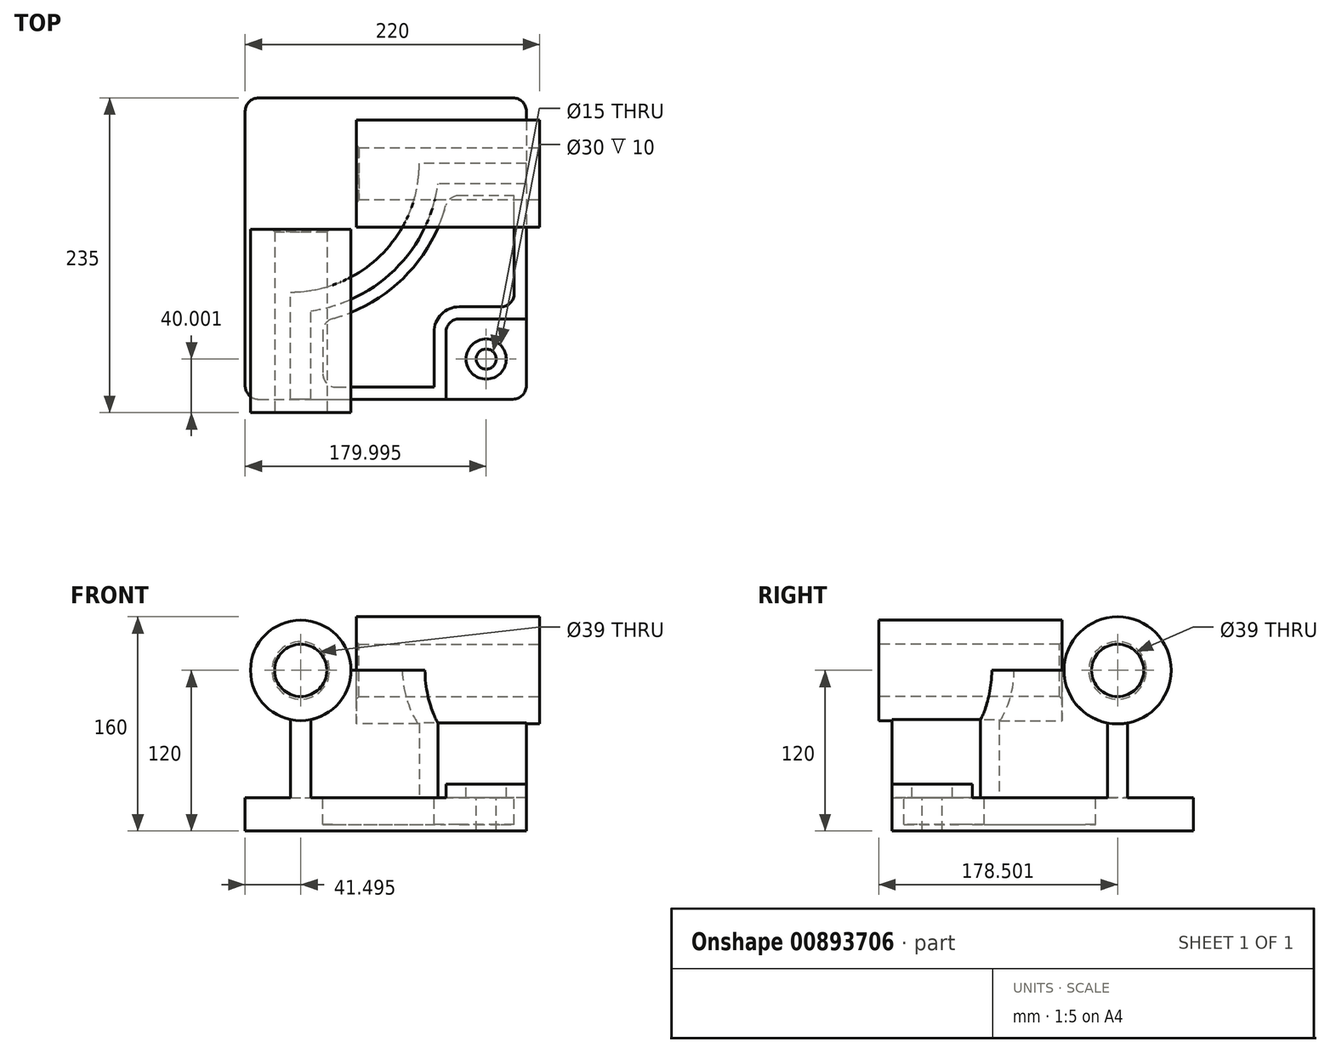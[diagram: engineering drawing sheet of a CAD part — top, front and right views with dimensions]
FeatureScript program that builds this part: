
annotation { "Feature Type Name" : "Feature", "Feature Type Description" : "" }
export const myFeature = defineFeature(function(context is Context, id is Id, definition is map)
    precondition{}
    {
        {
            var Q0;
            Q0=qCreatedBy(makeId("Top.planeOp"),FACE);
            var sketch = newSketch(context, id + "F0", { "sketchPlane" : qUnion([Q0])});
            skLineSegment(sketch, "E0.bottom", {"start": v(-141.63, 109.9) * mm, "end": v(68.37, 109.9) * mm});
            skLineSegment(sketch, "E0.top", {"start": v(-141.63, -115.1) * mm, "end": v(68.37, -115.1) * mm});
            skLineSegment(sketch, "E0.left", {"start": v(-141.63, 109.9) * mm, "end": v(-141.63, -115.1) * mm});
            skLineSegment(sketch, "E0.right", {"start": v(68.37, 109.9) * mm, "end": v(68.37, -115.1) * mm});
            skSolve(sketch);
        }
        {
            var Q0;
            Q0=makeQuery(id+"F0.imprint","IMPRINT",FACE,{"disambiguationData":[TD([[makeQuery(id+"F0.imprint","IMPRINT",EDGE,{"derivedFrom":sQuery(id+"F0.wireOp",EDGE,"E0.bottom")}),-1.0]])]});
            extrude(context, id + "F1", {"entities" : qUnion([Q0]), "depth" : 25 * mm, "offsetDistance" : 25 * mm});
        }
        {
            var Q0;
            Q0=makeQuery(id+"F1.opExtrude","CAP_FACE",FACE,{"disambiguationData":[OSD([sQuery(id+"F0.wireOp",EDGE,"E0.bottom"),sQuery(id+"F0.wireOp",EDGE,"E0.top"),sQuery(id+"F0.wireOp",EDGE,"E0.left"),sQuery(id+"F0.wireOp",EDGE,"E0.right")])],"isStart":false});
            var sketch = newSketch(context, id + "F2", { "sketchPlane" : qUnion([Q0])});
            skLineSegment(sketch, "E1", {"start": v(68.37, 60.9) * mm, "end": v(-11.63, 60.9) * mm});
            skLineSegment(sketch, "E2", {"start": v(-107.63, -115.1) * mm, "end": v(-107.63, -35.1) * mm});
            skArc(sketch, "E3", {"start": v(-107.63, -35.1) * mm, "mid": v(-39.75, -7) * mm, "end": v(-11.63, 60.9) * mm});
            skLineSegment(sketch, "E4", {"start": v(-107.63, 60.9) * mm, "end": v(-11.63, 60.9) * mm, "construction": true});
            skLineSegment(sketch, "E5", {"start": v(-107.63, 60.9) * mm, "end": v(-107.63, -35.1) * mm, "construction": true});
            skLineSegment(sketch, "E6.0", {"start": v(-92.63, -115.1) * mm, "end": v(-92.63, -49.1) * mm});
            skArc(sketch, "E6.1", {"start": v(-92.63, -49.1) * mm, "mid": v(-29.15, -17.6) * mm, "end": v(2.35, 45.9) * mm});
            skLineSegment(sketch, "E6.2", {"start": v(68.37, 45.9) * mm, "end": v(2.35, 45.9) * mm});
            skLineSegment(sketch, "E7.0", {"start": v(68.37, 109.9) * mm, "end": v(68.37, -115.1) * mm});
            skLineSegment(sketch, "E8.0", {"start": v(-141.63, 109.9) * mm, "end": v(68.37, 109.9) * mm});
            skSolve(sketch);
        }
        {
            var Q0;
            {var subQ3=sQuery(id+"F2.wireOp",EDGE,"E1");Q0=makeQuery(id+"F2.imprint","IMPRINT",FACE,{"disambiguationData":[TD([[makeQuery(id+"F2.imprint","IMPRINT",EDGE,{"derivedFrom":subQ3}),1.0]])]});}
            extrude(context, id + "F3", {"entities" : qUnion([Q0]), "operationType" : NewBodyOperationType.ADD, "depth" : 95 * mm, "offsetDistance" : 25 * mm});
        }
        {
            var Q0;
            {var subQ0=sQuery(id+"F0.wireOp",EDGE,"E0.top");Q0=makeQuery(id+"F3.boolean.opBoolean","MERGE",FACE,{"derivedFrom":[makeQuery(id+"F1.opExtrude","SWEPT_FACE",FACE,{"disambiguationData":[OSD([subQ0])]}),makeQuery(id+"F3.opExtrude","SWEPT_FACE",FACE,{"disambiguationData":[OSD([subQ0])]})]});}
            var sketch = newSketch(context, id + "F4", { "sketchPlane" : qUnion([Q0])});
            skCircle(sketch, "E9", {"center": v(-100.13, 120) * mm, "radius": 37.5 * mm});
            skSolve(sketch);
        }
        {
            var Q0;
            Q0 = qSketchRegion(id + "F4", true);
            extrude(context, id + "F5", {"entities" : qUnion([Q0]), "operationType" : NewBodyOperationType.ADD, "depth" : 10 * mm, "offsetDistance" : 25 * mm, "hasSecondDirection" : true, "secondDirectionOppositeDirection" : true, "secondDirectionDepth" : (137 - 10) * mm});
        }
        {
            var Q0;
            Q0=makeQuery(id+"F3.boolean.opBoolean","MERGE",FACE,{"derivedFrom":[makeQuery(id+"F1.opExtrude","SWEPT_FACE",FACE,{"disambiguationData":[OSD([sQuery(id+"F0.wireOp",EDGE,"E0.right")])]}),makeQuery(id+"F3.opExtrude","SWEPT_FACE",FACE,{"disambiguationData":[OSD([sQuery(id+"F2.wireOp",EDGE,"E7.0")])]})]});
            var sketch = newSketch(context, id + "F6", { "sketchPlane" : qUnion([Q0])});
            skCircle(sketch, "E10", {"center": v(53.4, 120) * mm, "radius": 40 * mm});
            skSolve(sketch);
        }
        {
            var Q0;
            {var subQ1=sQuery(id+"F2.wireOp",EDGE,"E7.0");var subQ6=makeQuery(id+"F3.opExtrude","CAP_EDGE",EDGE,{"disambiguationData":[OSD([subQ1])],"isStart":false});Q0=makeQuery(id+"F6.imprint","IMPRINT",FACE,{"disambiguationData":[TD([[makeQuery(id+"F6.imprint","IMPRINT",EDGE,{"derivedFrom":subQ6}),-1.0]])]});}
            var Q1;
            {var subQ1=sQuery(id+"F2.wireOp",EDGE,"E7.0");var subQ6=makeQuery(id+"F3.opExtrude","CAP_EDGE",EDGE,{"disambiguationData":[OSD([subQ1])],"isStart":false});Q1=makeQuery(id+"F6.imprint","IMPRINT",FACE,{"disambiguationData":[TD([[makeQuery(id+"F6.imprint","IMPRINT",EDGE,{"derivedFrom":subQ6}),1.0]])]});}
            extrude(context, id + "F7", {"entities" : qUnion([Q0, Q1]), "operationType" : NewBodyOperationType.ADD, "depth" : 10 * mm, "offsetDistance" : 25 * mm, "hasSecondDirection" : true, "secondDirectionOppositeDirection" : true, "secondDirectionDepth" : 127 * mm});
        }
        {
            var Q0;
            {var subQ0=sQuery(id+"F0.wireOp",EDGE,"E0.right");var subQ1=sQuery(id+"F0.wireOp",EDGE,"E0.top");Q0=makeQuery(id+"F3.boolean.opBoolean","SPLIT",FACE,{"disambiguationData":[TD([makeQuery(id+"F3.opExtrude","SWEPT_FACE",FACE,{"disambiguationData":[OSD([sQuery(id+"F2.wireOp",EDGE,"E6.0")])]})])],"derivedFrom":makeQuery(id+"F1.opExtrude","CAP_FACE",FACE,{"disambiguationData":[OSD([sQuery(id+"F0.wireOp",EDGE,"E0.bottom"),subQ1,sQuery(id+"F0.wireOp",EDGE,"E0.left"),subQ0])],"isStart":false})});}
            var sketch = newSketch(context, id + "F8", { "sketchPlane" : qUnion([Q0])});
            skLineSegment(sketch, "E11.bottom", {"start": v(68.37, -115.1) * mm, "end": v(8.37, -115.1) * mm});
            skLineSegment(sketch, "E11.top", {"start": v(68.37, -55.1) * mm, "end": v(8.37, -55.1) * mm});
            skLineSegment(sketch, "E11.left", {"start": v(68.37, -115.1) * mm, "end": v(68.37, -55.1) * mm});
            skLineSegment(sketch, "E11.right", {"start": v(8.37, -115.1) * mm, "end": v(8.37, -55.1) * mm});
            skSolve(sketch);
        }
        {
            var Q0;
            Q0 = qSketchRegion(id + "F8", true);
            extrude(context, id + "F9", {"entities" : qUnion([Q0]), "operationType" : NewBodyOperationType.ADD, "depth" : 10 * mm, "offsetDistance" : 25 * mm});
        }
        {
            var Q0;
            Q0=makeQuery(id+"F9.opExtrude","SWEPT_EDGE",EDGE,{"disambiguationData":[OSD([sQuery(id+"F8.wireOp",EDGE,"E11.top"),sQuery(id+"F8.wireOp",EDGE,"E11.right")])]});
            fillet(context, id + "F10", {"entities" : qUnion([Q0]), "radius" : 10 * mm, "tangentPropagation" : true, "allowEdgeOverflow" : false});
        }
        {
            var Q0;
            {var subQ0=sQuery(id+"F0.wireOp",EDGE,"E0.right");var subQ1=sQuery(id+"F0.wireOp",EDGE,"E0.top");Q0=makeQuery(id+"F3.boolean.opBoolean","SPLIT",FACE,{"disambiguationData":[TD([makeQuery(id+"F3.opExtrude","SWEPT_FACE",FACE,{"disambiguationData":[OSD([sQuery(id+"F2.wireOp",EDGE,"E6.0")])]})])],"derivedFrom":makeQuery(id+"F1.opExtrude","CAP_FACE",FACE,{"disambiguationData":[OSD([sQuery(id+"F0.wireOp",EDGE,"E0.bottom"),subQ1,sQuery(id+"F0.wireOp",EDGE,"E0.left"),subQ0])],"isStart":false})});}
            var sketch = newSketch(context, id + "F11", { "sketchPlane" : qUnion([Q0])});
            skLineSegment(sketch, "E12.0", {"start": v(-83.63, -56.68) * mm, "end": v(-83.63, -106.1) * mm});
            skArc(sketch, "E12.1", {"start": v(9.94, 36.9) * mm, "mid": v(-22.78, -23.96) * mm, "end": v(-83.63, -56.68) * mm});
            skLineSegment(sketch, "E12.2", {"start": v(-83.63, -106.1) * mm, "end": v(-0.63, -106.1) * mm});
            skLineSegment(sketch, "E12.3", {"start": v(59.37, 36.9) * mm, "end": v(9.94, 36.9) * mm});
            skLineSegment(sketch, "E12.4", {"start": v(-0.63, -106.1) * mm, "end": v(-0.63, -65.1) * mm});
            skArc(sketch, "E12.5", {"start": v(-0.63, -65.1) * mm, "mid": v(4.93, -51.67) * mm, "end": v(18.37, -46.1) * mm});
            skLineSegment(sketch, "E12.6", {"start": v(18.37, -46.1) * mm, "end": v(59.37, -46.1) * mm});
            skLineSegment(sketch, "E12.7", {"start": v(59.37, -46.1) * mm, "end": v(59.37, 36.9) * mm});
            skSolve(sketch);
        }
        {
            var Q0;
            Q0=makeQuery(id+"F11.imprint","IMPRINT",FACE,{"disambiguationData":[TD([[makeQuery(id+"F11.imprint","IMPRINT",EDGE,{"derivedFrom":sQuery(id+"F11.wireOp",EDGE,"E12.0")}),1.0]])]});
            extrude(context, id + "F12", {"entities" : qUnion([Q0]), "operationType" : NewBodyOperationType.REMOVE, "oppositeDirection" : true, "depth" : 20 * mm, "offsetDistance" : 25 * mm});
        }
        {
            var Q0;
            Q0=makeQuery(id+"F9.opExtrude","CAP_FACE",FACE,{"disambiguationData":[OSD([sQuery(id+"F8.wireOp",EDGE,"E11.bottom"),sQuery(id+"F8.wireOp",EDGE,"E11.top"),sQuery(id+"F8.wireOp",EDGE,"E11.left"),sQuery(id+"F8.wireOp",EDGE,"E11.right")])],"isStart":false});
            var sketch = newSketch(context, id + "F13", { "sketchPlane" : qUnion([Q0])});
            skCircle(sketch, "E13", {"center": v(38.37, -85.1) * mm, "radius": 15 * mm});
            skPoint(sketch, "E13.centerSnap0", {"position": v(68.37, -85.1) * mm});
            skPoint(sketch, "E13.centerSnap1", {"position": v(38.37, -115.1) * mm});
            skSolve(sketch);
        }
        {
            var Q0;
            Q0=sQuery(id+"F13.wireOp",VERTEX,"E13.center");
            var Q1;
            Q1=makeQuery(id+"F1.opExtrude","SWEPT_BODY",BODY,{"disambiguationData":[OSD([sQuery(id+"F0.wireOp",EDGE,"E0.bottom"),sQuery(id+"F0.wireOp",EDGE,"E0.top"),sQuery(id+"F0.wireOp",EDGE,"E0.left"),sQuery(id+"F0.wireOp",EDGE,"E0.right")])]});
            hole(context, id + "F14", {"style" : HoleStyle.C_BORE, "endStyle" : HoleEndStyle.THROUGH, "holeDiameter" : 15 * mm, "cBoreDiameter" : 30 * mm, "cBoreDepth" : 10 * mm, "majorDiameter" : 5 * mm, "isTappedThrough" : true, "tappedDepth" : 12 * mm, "tapClearance" : 3, "locations" : qUnion([Q0]), "scope" : qUnion([Q1])});
        }
        {
            var Q0;
            Q0=makeQuery(id+"F12.boolean.opBoolean","COPY",EDGE,{"derivedFrom":makeQuery(id+"F12.opExtrude","SWEPT_EDGE",EDGE,{"disambiguationData":[OSD([sQuery(id+"F11.wireOp",EDGE,"E12.0"),sQuery(id+"F11.wireOp",EDGE,"E12.1")])]})});
            var Q1;
            Q1=makeQuery(id+"F12.boolean.opBoolean","COPY",EDGE,{"derivedFrom":makeQuery(id+"F12.opExtrude","SWEPT_EDGE",EDGE,{"disambiguationData":[OSD([sQuery(id+"F11.wireOp",EDGE,"E12.1"),sQuery(id+"F11.wireOp",EDGE,"E12.3")])]})});
            var Q2;
            Q2=makeQuery(id+"F12.boolean.opBoolean","COPY",EDGE,{"derivedFrom":makeQuery(id+"F12.opExtrude","SWEPT_EDGE",EDGE,{"disambiguationData":[OSD([sQuery(id+"F11.wireOp",EDGE,"E12.0"),sQuery(id+"F11.wireOp",EDGE,"E12.2")])]})});
            var Q3;
            Q3=makeQuery(id+"F12.boolean.opBoolean","COPY",EDGE,{"derivedFrom":makeQuery(id+"F12.opExtrude","SWEPT_EDGE",EDGE,{"disambiguationData":[OSD([sQuery(id+"F11.wireOp",EDGE,"E12.6"),sQuery(id+"F11.wireOp",EDGE,"E12.7")])]})});
            fillet(context, id + "F15", {"entities" : qUnion([Q0, Q1, Q2, Q3]), "radius" : 10 * mm, "tangentPropagation" : true, "allowEdgeOverflow" : false});
        }
        {
            var Q0;
            Q0=makeQuery(id+"F5.opExtrude","CAP_FACE",FACE,{"disambiguationData":[OSD([sQuery(id+"F4.wireOp",EDGE,"E9")])],"isStart":false});
            var sketch = newSketch(context, id + "F16", { "sketchPlane" : qUnion([Q0])});
            skCircle(sketch, "E14", {"center": v(-100.13, 120) * mm, "radius": 19.5 * mm});
            skSolve(sketch);
        }
        {
            var Q0;
            Q0=makeQuery(id+"F7.opExtrude","CAP_FACE",FACE,{"disambiguationData":[OSD([sQuery(id+"F6.wireOp",EDGE,"E10")])],"isStart":false});
            var sketch = newSketch(context, id + "F17", { "sketchPlane" : qUnion([Q0])});
            skCircle(sketch, "E15", {"center": v(53.4, 120) * mm, "radius": 19.5 * mm});
            skSolve(sketch);
        }
        {
            var Q0;
            Q0 = qSketchRegion(id + "F17", true);
            extrude(context, id + "F18", {"entities" : qUnion([Q0]), "operationType" : NewBodyOperationType.REMOVE, "endBound" : BoundingType.THROUGH_ALL, "oppositeDirection" : true, "depth" : 25 * mm, "offsetDistance" : 25 * mm});
        }
        {
            var Q0;
            Q0=makeQuery(id+"F16.imprint","IMPRINT",FACE,{"disambiguationData":[TD([[makeQuery(id+"F16.imprint","IMPRINT",EDGE,{"derivedFrom":sQuery(id+"F16.wireOp",EDGE,"E14")}),1.0]])]});
            var Q1;
            Q1=sQuery(id+"F16.wireOp",EDGE,"E14");
            extrude(context, id + "F19", {"entities" : qUnion([Q0]), "operationType" : NewBodyOperationType.REMOVE, "surfaceEntities" : qUnion([Q1]), "endBound" : BoundingType.THROUGH_ALL, "oppositeDirection" : true, "depth" : 25 * mm, "offsetDistance" : 25 * mm});
        }
        {
            var Q0;
            Q0=makeQuery(id+"F19.boolean.opBoolean","COPY",EDGE,{"derivedFrom":makeQuery(id+"F19.opExtrude","CAP_EDGE",EDGE,{"disambiguationData":[OSD([sQuery(id+"F16.wireOp",EDGE,"E14")])],"isStart":true})});
            var Q1;
            Q1=makeQuery(id+"F18.boolean.opBoolean","COPY",EDGE,{"derivedFrom":makeQuery(id+"F18.opExtrude","CAP_EDGE",EDGE,{"disambiguationData":[OSD([sQuery(id+"F17.wireOp",EDGE,"E15")])],"isStart":true})});
            var Q2;
            Q2=makeQuery(id+"F19.boolean.opBoolean","INTERSECT",EDGE,{"derivedFrom":[makeQuery(id+"F5.opExtrude","CAP_FACE",FACE,{"disambiguationData":[OSD([sQuery(id+"F4.wireOp",EDGE,"E9")])],"isStart":true}),makeQuery(id+"F19.opExtrude","SWEPT_FACE",FACE,{"disambiguationData":[OSD([sQuery(id+"F16.wireOp",EDGE,"E14")])]})]});
            var Q3;
            Q3=makeQuery(id+"F18.boolean.opBoolean","INTERSECT",EDGE,{"derivedFrom":[makeQuery(id+"F7.opExtrude","CAP_FACE",FACE,{"disambiguationData":[OSD([sQuery(id+"F6.wireOp",EDGE,"E10")])],"isStart":true}),makeQuery(id+"F18.opExtrude","SWEPT_FACE",FACE,{"disambiguationData":[OSD([sQuery(id+"F17.wireOp",EDGE,"E15")])]})]});
            chamfer(context, id + "F20", {"entities" : qUnion([Q0, Q1, Q2, Q3]), "width" : 2 * mm, "tangentPropagation" : true});
        }
        {
            var Q0;
            Q0=makeQuery(id+"F9.boolean.opBoolean","MERGE",EDGE,{"derivedFrom":[makeQuery(id+"F1.opExtrude","SWEPT_EDGE",EDGE,{"disambiguationData":[OSD([sQuery(id+"F0.wireOp",EDGE,"E0.top"),sQuery(id+"F0.wireOp",EDGE,"E0.right")])]}),makeQuery(id+"F9.opExtrude","SWEPT_EDGE",EDGE,{"disambiguationData":[OSD([sQuery(id+"F8.wireOp",EDGE,"E11.bottom"),sQuery(id+"F8.wireOp",EDGE,"E11.left")])]})]});
            var Q1;
            Q1=makeQuery(id+"F1.opExtrude","SWEPT_EDGE",EDGE,{"disambiguationData":[OSD([sQuery(id+"F0.wireOp",EDGE,"E0.top"),sQuery(id+"F0.wireOp",EDGE,"E0.left")])]});
            var Q2;
            Q2=makeQuery(id+"F1.opExtrude","SWEPT_EDGE",EDGE,{"disambiguationData":[OSD([sQuery(id+"F0.wireOp",EDGE,"E0.bottom"),sQuery(id+"F0.wireOp",EDGE,"E0.right")])]});
            var Q3;
            Q3=makeQuery(id+"F1.opExtrude","SWEPT_EDGE",EDGE,{"disambiguationData":[OSD([sQuery(id+"F0.wireOp",EDGE,"E0.bottom"),sQuery(id+"F0.wireOp",EDGE,"E0.left")])]});
            fillet(context, id + "F21", {"entities" : qUnion([Q0, Q1, Q2, Q3]), "radius" : 10 * mm, "tangentPropagation" : true, "allowEdgeOverflow" : false});
        }
    });
